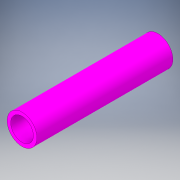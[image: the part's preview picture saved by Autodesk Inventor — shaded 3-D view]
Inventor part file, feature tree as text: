
AUTODESK INVENTOR PART (.ipt)
format: ipt  version: 2018 (Build 220112000, 112)  size: 107,008 bytes
history: native  units: in
note: dims shown in document units (in); Inventor stores cm internally (conversion verified against a paired STEP export)
features: extrude x1, sketch x1
ambient origin geometry x8: Origin, YZ Plane, XZ Plane, XY Plane, X Axis, Y Axis, Z Axis, Center Point
bodies: Solid1 (feature_tree)
feature tree (2):
  extrude  "Extrusion1"  Depth=6.0in
  sketch  "Sketch1"  dims[d0=1.315in d1=1.0in d2=6.0in d3=0.0in]
